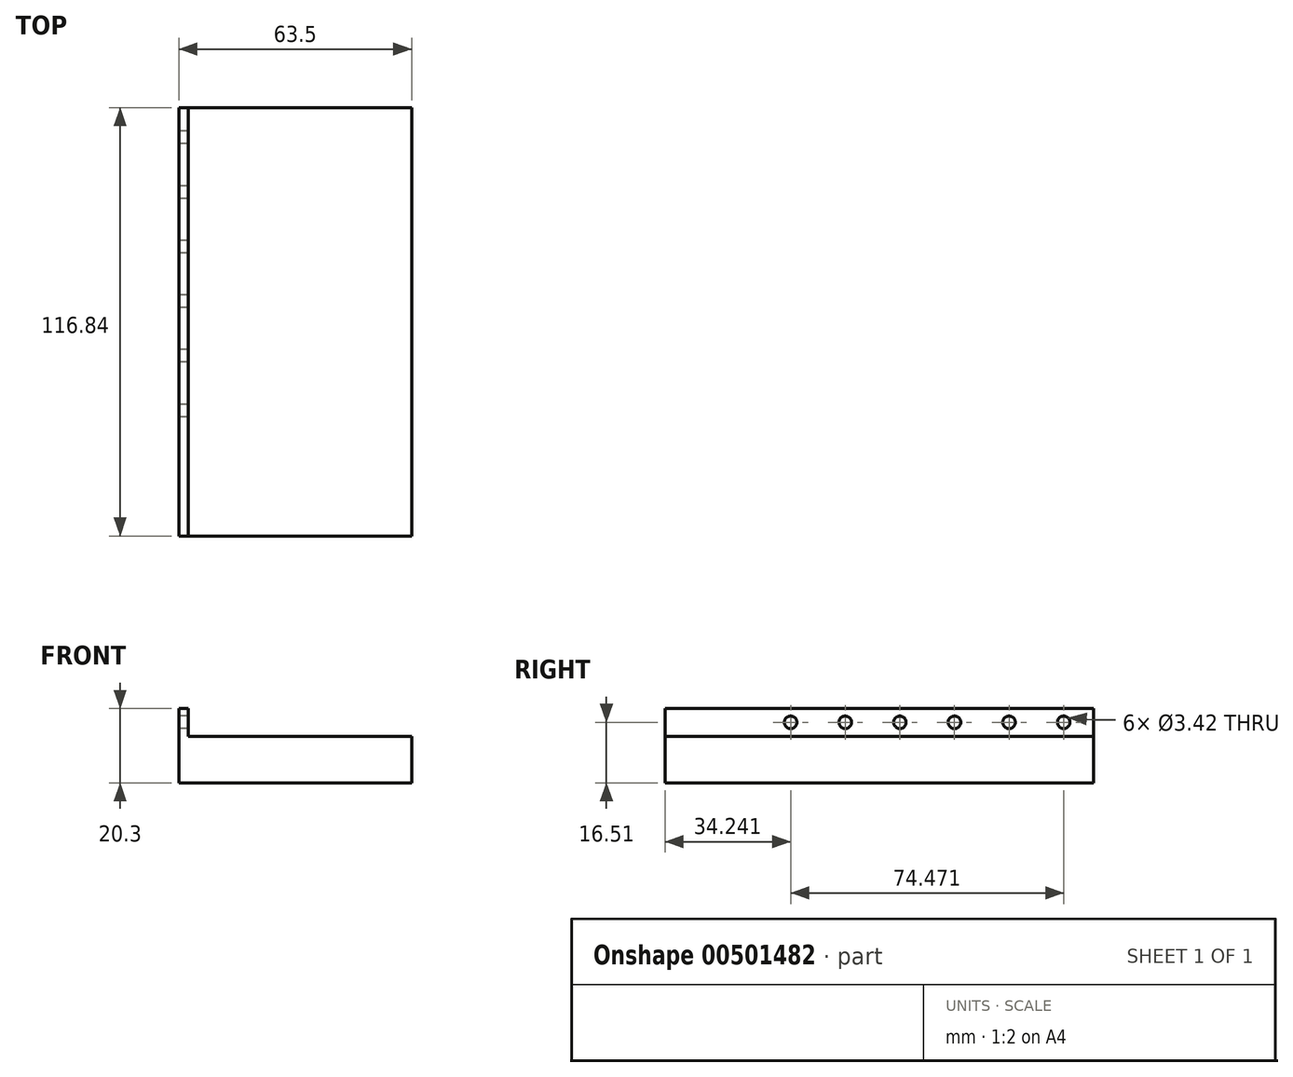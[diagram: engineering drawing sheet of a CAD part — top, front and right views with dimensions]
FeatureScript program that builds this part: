
annotation { "Feature Type Name" : "Feature", "Feature Type Description" : "" }
export const myFeature = defineFeature(function(context is Context, id is Id, definition is map)
    precondition{}
    {
        {
            var Q0;
            Q0=qCreatedBy(makeId("Top.planeOp"),FACE);
            var sketch = newSketch(context, id + "F0", { "sketchPlane" : qUnion([Q0])});
            skLineSegment(sketch, "E0.bottom", {"start": v(-31.75, 58.42) * mm, "end": v(31.75, 58.42) * mm});
            skLineSegment(sketch, "E0.top", {"start": v(-31.75, -58.42) * mm, "end": v(31.75, -58.42) * mm});
            skLineSegment(sketch, "E0.left", {"start": v(-31.75, 58.42) * mm, "end": v(-31.75, -58.42) * mm});
            skLineSegment(sketch, "E0.right", {"start": v(31.75, 58.42) * mm, "end": v(31.75, -58.42) * mm});
            skPoint(sketch, "E1", {"position": v(31.75, 0) * mm});
            skPoint(sketch, "E2", {"position": v(0, 58.42) * mm});
            skSolve(sketch);
        }
        {
            var Q0;
            Q0=makeQuery(id+"F0.imprint","IMPRINT",FACE,{"disambiguationData":[TD([[makeQuery(id+"F0.imprint","IMPRINT",EDGE,{"derivedFrom":sQuery(id+"F0.wireOp",EDGE,"E0.bottom")}),-1.0]])]});
            extrude(context, id + "F1", {"entities" : qUnion([Q0]), "depth" : 12.7 * mm});
        }
        {
            var Q0;
            Q0=makeQuery(id+"F1.opExtrude","SWEPT_FACE",FACE,{"disambiguationData":[OSD([sQuery(id+"F0.wireOp",EDGE,"E0.left")])]});
            var sketch = newSketch(context, id + "F2", { "sketchPlane" : qUnion([Q0])});
            skLineSegment(sketch, "E3.bottom", {"start": v(58.42, 12.7) * mm, "end": v(-58.42, 12.7) * mm});
            skLineSegment(sketch, "E3.top", {"start": v(58.42, 20.3) * mm, "end": v(-58.42, 20.3) * mm});
            skLineSegment(sketch, "E3.left", {"start": v(58.42, 12.7) * mm, "end": v(58.42, 20.3) * mm});
            skLineSegment(sketch, "E3.right", {"start": v(-58.42, 12.7) * mm, "end": v(-58.42, 20.3) * mm});
            skCircle(sketch, "E4", {"center": v(-50.3, 16.5) * mm, "radius": 1.7 * mm});
            skCircle(sketch, "E5.1.0.0", {"center": v(-35.4, 16.5) * mm, "radius": 1.7 * mm});
            skCircle(sketch, "E5.2.0.0", {"center": v(-20.5, 16.5) * mm, "radius": 1.7 * mm});
            skCircle(sketch, "E5.3.0.0", {"center": v(-5.6, 16.5) * mm, "radius": 1.7 * mm});
            skCircle(sketch, "E5.4.0.0", {"center": v(9.28, 16.5) * mm, "radius": 1.7 * mm});
            skCircle(sketch, "E5.5.0.0", {"center": v(24.18, 16.5) * mm, "radius": 1.7 * mm});
            skLineSegment(sketch, "E5.direction1", {"start": v(-50.3, 16.51) * mm, "end": v(-35.4, 16.51) * mm, "construction": true});
            skSolve(sketch);
        }
        {
            var Q0;
            Q0=makeQuery(id+"F2.imprint","IMPRINT",FACE,{"disambiguationData":[TD([[makeQuery(id+"F2.imprint","IMPRINT",EDGE,{"derivedFrom":sQuery(id+"F2.wireOp",EDGE,"E3.bottom")}),1.0]])]});
            extrude(context, id + "F3", {"entities" : qUnion([Q0]), "operationType" : NewBodyOperationType.ADD, "oppositeDirection" : true, "depth" : 2.54 * mm});
        }
    });
